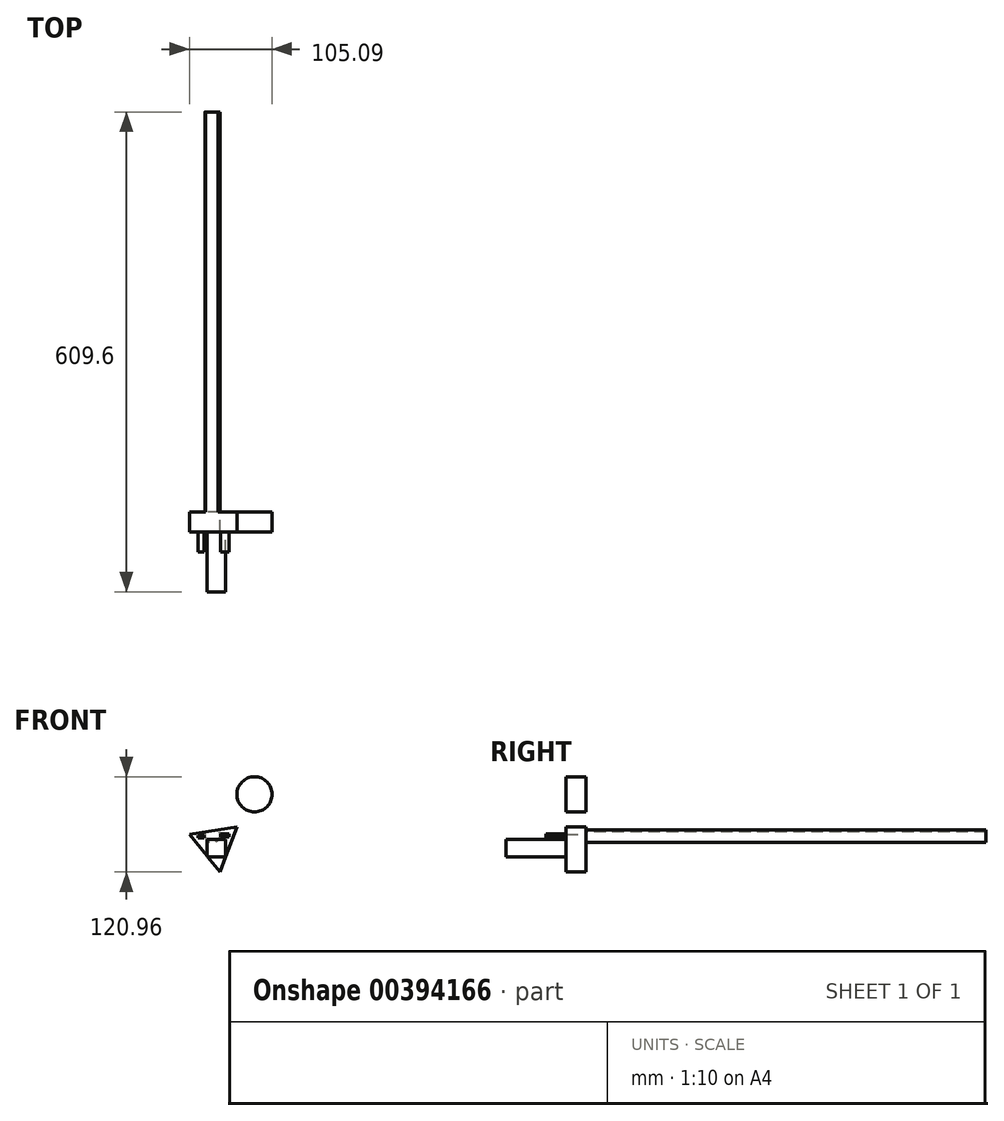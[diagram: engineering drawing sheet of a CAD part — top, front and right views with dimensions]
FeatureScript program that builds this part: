
annotation { "Feature Type Name" : "Feature", "Feature Type Description" : "" }
export const myFeature = defineFeature(function(context is Context, id is Id, definition is map)
    precondition{}
    {
        {
            var Q0;
            Q0=qCreatedBy(makeId("Front.planeOp"),FACE);
            var sketch = newSketch(context, id + "F0", { "sketchPlane" : qUnion([Q0])});
            skCircle(sketch, "E0", {"center": v(-39.51, 36.75) * mm, "radius": 31.41 * mm});
            skCircle(sketch, "E1", {"center": v(24.34, 44.64) * mm, "radius": 22.32 * mm});
            skSolve(sketch);
        }
        {
            var Q0;
            Q0=qCreatedBy(makeId("Front.planeOp"),FACE);
            var sketch = newSketch(context, id + "F1", { "sketchPlane" : qUnion([Q0])});
            skCircle(sketch, "E2.cCircle", {"center": v(-25.32, -19.02) * mm, "radius": 17.71 * mm, "construction": true});
            skLineSegment(sketch, "E2.0", {"start": v(2.15, 3.35) * mm, "end": v(-19.7, -54) * mm});
            skLineSegment(sketch, "E2.1", {"start": v(-19.7, -54) * mm, "end": v(-58.43, -6.4) * mm});
            skLineSegment(sketch, "E2.2", {"start": v(-58.43, -6.4) * mm, "end": v(2.15, 3.35) * mm});
            skPoint(sketch, "E2.0.midPoint", {"position": v(-8.77, -25.32) * mm});
            skCircle(sketch, "E3.cCircle", {"center": v(-112.43, 22.17) * mm, "radius": 6.09 * mm, "construction": true});
            skLineSegment(sketch, "E3.0", {"start": v(-124.6, 22.37) * mm, "end": v(-106.17, 32.61) * mm});
            skLineSegment(sketch, "E3.1", {"start": v(-106.17, 32.61) * mm, "end": v(-106.52, 11.53) * mm});
            skLineSegment(sketch, "E3.2", {"start": v(-106.52, 11.53) * mm, "end": v(-124.6, 22.37) * mm});
            skPoint(sketch, "E3.0.midPoint", {"position": v(-115.38, 27.5) * mm});
            skSolve(sketch);
        }
        {
            var Q0;
            Q0=makeQuery(id+"F0.imprint","IMPRINT",FACE,{"disambiguationData":[TD([[makeQuery(id+"F0.imprint","IMPRINT",EDGE,{"derivedFrom":sQuery(id+"F0.wireOp",EDGE,"E1")}),1.0]])]});
            var Q1;
            Q1=makeQuery(id+"F1.imprint","IMPRINT",FACE,{"disambiguationData":[TD([[makeQuery(id+"F1.imprint","IMPRINT",EDGE,{"derivedFrom":sQuery(id+"F1.wireOp",EDGE,"E2.0")}),-1.0]])]});
            extrude(context, id + "F2", {"entities" : qUnion([Q0, Q1]), "depth" : 25.4 * mm, "offsetDistance" : 25.4 * mm});
        }
        {
            var Q0;
            Q0=makeQuery(id+"F2.opExtrude","CAP_FACE",FACE,{"disambiguationData":[OSD([sQuery(id+"F1.wireOp",EDGE,"E2.0"),sQuery(id+"F1.wireOp",EDGE,"E2.1"),sQuery(id+"F1.wireOp",EDGE,"E2.2")])],"isStart":true});
            var sketch = newSketch(context, id + "F3", { "sketchPlane" : qUnion([Q0])});
            skCircle(sketch, "E4", {"center": v(28.98, -7.02) * mm, "radius": 9.53 * mm});
            skSolve(sketch);
        }
        {
            var Q0;
            {var subQ0=sQuery(id+"F3.wireOp",EDGE,"E4");var subQ1=makeQuery(id+"F2.opExtrude","CAP_EDGE",EDGE,{"disambiguationData":[OSD([sQuery(id+"F1.wireOp",EDGE,"E2.2")])],"isStart":true});var subQ2=makeQuery(id+"F3.imprint","INTERSECT",VERTEX,{"disambiguationData":[OD(0.0)],"derivedFrom":[subQ1,subQ0]});Q0=makeQuery(id+"F3.imprint","IMPRINT",FACE,{"disambiguationData":[TD([[makeQuery(id+"F3.imprint","IMPRINT",EDGE,{"disambiguationData":[TD([[subQ2,-1.0]])],"derivedFrom":subQ0}),1.0]])]});}
            extrude(context, id + "F4", {"entities" : qUnion([Q0]), "operationType" : NewBodyOperationType.ADD, "depth" : 508 * mm, "offsetDistance" : 25.4 * mm});
        }
        {
            var Q0;
            Q0=makeQuery(id+"F2.opExtrude","CAP_FACE",FACE,{"disambiguationData":[OSD([sQuery(id+"F1.wireOp",EDGE,"E2.0"),sQuery(id+"F1.wireOp",EDGE,"E2.1"),sQuery(id+"F1.wireOp",EDGE,"E2.2")])],"isStart":false});
            var sketch = newSketch(context, id + "F5", { "sketchPlane" : qUnion([Q0])});
            skLineSegment(sketch, "E5.bottom", {"start": v(-36.23, -12.63) * mm, "end": v(-12.5, -12.63) * mm});
            skLineSegment(sketch, "E5.top", {"start": v(-36.23, -35.1) * mm, "end": v(-12.5, -35.1) * mm});
            skLineSegment(sketch, "E5.left", {"start": v(-36.23, -12.63) * mm, "end": v(-36.23, -35.1) * mm});
            skLineSegment(sketch, "E5.right", {"start": v(-12.5, -12.63) * mm, "end": v(-12.5, -35.1) * mm});
            skSolve(sketch);
        }
        {
            var Q0;
            {var subQ1=sQuery(id+"F5.wireOp",EDGE,"E5.bottom");Q0=makeQuery(id+"F5.imprint","IMPRINT",FACE,{"disambiguationData":[TD([[makeQuery(id+"F5.imprint","IMPRINT",EDGE,{"derivedFrom":subQ1}),-1.0]])]});}
            extrude(context, id + "F6", {"entities" : qUnion([Q0]), "operationType" : NewBodyOperationType.ADD, "depth" : 76.2 * mm, "offsetDistance" : 25.4 * mm});
        }
        {
            var Q0;
            {var subQ0=sQuery(id+"F1.wireOp",EDGE,"E2.2");var subQ1=sQuery(id+"F1.wireOp",EDGE,"E2.1");var subQ2=sQuery(id+"F1.wireOp",EDGE,"E2.0");var subQ3=makeQuery(id+"F2.opExtrude","CAP_FACE",FACE,{"disambiguationData":[OSD([subQ2,subQ1,subQ0])],"isStart":false});Q0=makeQuery(id+"F6.boolean.opBoolean","SPLIT",FACE,{"disambiguationData":[TD([makeQuery(id+"F2.opExtrude","SWEPT_FACE",FACE,{"disambiguationData":[OSD([subQ2])]}),subQ3,makeQuery(id+"F2.opExtrude","SWEPT_FACE",FACE,{"disambiguationData":[OSD([subQ1])]}),makeQuery(id+"F2.opExtrude","SWEPT_FACE",FACE,{"disambiguationData":[OSD([subQ0])]}),makeQuery(id+"F4.opExtrude","SWEPT_FACE",FACE,{"disambiguationData":[OSD([subQ0])]}),makeQuery(id+"F6.opExtrude","SWEPT_FACE",FACE,{"disambiguationData":[OSD([sQuery(id+"F5.wireOp",EDGE,"E5.bottom")])]}),makeQuery(id+"F6.opExtrude","SWEPT_FACE",FACE,{"disambiguationData":[OSD([sQuery(id+"F5.wireOp",EDGE,"E5.top")])]}),makeQuery(id+"F6.opExtrude","SWEPT_FACE",FACE,{"disambiguationData":[OSD([sQuery(id+"F5.wireOp",EDGE,"E5.left")])]}),makeQuery(id+"F6.opExtrude","SWEPT_FACE",FACE,{"disambiguationData":[OSD([sQuery(id+"F5.wireOp",EDGE,"E5.right")])]}),makeQuery(id+"F6.opExtrude","SWEPT_FACE",FACE,{"disambiguationData":[OSD([subQ1])]})])],"derivedFrom":subQ3});}
            var sketch = newSketch(context, id + "F7", { "sketchPlane" : qUnion([Q0])});
            skLineSegment(sketch, "E6.bottom", {"start": v(-47.47, -7.47) * mm, "end": v(-39.91, -7.47) * mm});
            skLineSegment(sketch, "E6.top", {"start": v(-47.47, -10.42) * mm, "end": v(-39.91, -10.42) * mm});
            skLineSegment(sketch, "E6.left", {"start": v(-47.47, -7.47) * mm, "end": v(-47.47, -10.42) * mm});
            skLineSegment(sketch, "E6.right", {"start": v(-39.91, -7.47) * mm, "end": v(-39.91, -10.42) * mm});
            skLineSegment(sketch, "E7.bottom", {"start": v(-14.29, -4.89) * mm, "end": v(-6.73, -4.89) * mm});
            skLineSegment(sketch, "E7.top", {"start": v(-14.29, -7.47) * mm, "end": v(-6.73, -7.47) * mm});
            skLineSegment(sketch, "E7.left", {"start": v(-14.29, -4.89) * mm, "end": v(-14.29, -7.47) * mm});
            skLineSegment(sketch, "E7.right", {"start": v(-6.73, -4.89) * mm, "end": v(-6.73, -7.47) * mm});
            skSolve(sketch);
        }
        {
            var Q0;
            Q0=makeQuery(id+"F7.imprint","IMPRINT",FACE,{"disambiguationData":[TD([[makeQuery(id+"F7.imprint","IMPRINT",EDGE,{"derivedFrom":sQuery(id+"F7.wireOp",EDGE,"E6.bottom")}),-1.0]])]});
            extrude(context, id + "F8", {"entities" : qUnion([Q0]), "operationType" : NewBodyOperationType.ADD, "depth" : 25.4 * mm, "offsetDistance" : 25.4 * mm});
        }
        {
            var Q0;
            {var subQ0=sQuery(id+"F1.wireOp",EDGE,"E2.2");var subQ1=sQuery(id+"F1.wireOp",EDGE,"E2.1");var subQ2=sQuery(id+"F1.wireOp",EDGE,"E2.0");var subQ3=makeQuery(id+"F2.opExtrude","CAP_FACE",FACE,{"disambiguationData":[OSD([subQ2,subQ1,subQ0])],"isStart":false});Q0=makeQuery(id+"F6.boolean.opBoolean","SPLIT",FACE,{"disambiguationData":[TD([makeQuery(id+"F2.opExtrude","SWEPT_FACE",FACE,{"disambiguationData":[OSD([subQ2])]}),subQ3,makeQuery(id+"F2.opExtrude","SWEPT_FACE",FACE,{"disambiguationData":[OSD([subQ1])]}),makeQuery(id+"F2.opExtrude","SWEPT_FACE",FACE,{"disambiguationData":[OSD([subQ0])]}),makeQuery(id+"F4.opExtrude","SWEPT_FACE",FACE,{"disambiguationData":[OSD([subQ0])]}),makeQuery(id+"F6.opExtrude","SWEPT_FACE",FACE,{"disambiguationData":[OSD([sQuery(id+"F5.wireOp",EDGE,"E5.bottom")])]}),makeQuery(id+"F6.opExtrude","SWEPT_FACE",FACE,{"disambiguationData":[OSD([sQuery(id+"F5.wireOp",EDGE,"E5.top")])]}),makeQuery(id+"F6.opExtrude","SWEPT_FACE",FACE,{"disambiguationData":[OSD([sQuery(id+"F5.wireOp",EDGE,"E5.left")])]}),makeQuery(id+"F6.opExtrude","SWEPT_FACE",FACE,{"disambiguationData":[OSD([sQuery(id+"F5.wireOp",EDGE,"E5.right")])]}),makeQuery(id+"F6.opExtrude","SWEPT_FACE",FACE,{"disambiguationData":[OSD([subQ1])]})])],"derivedFrom":subQ3});}
            var sketch = newSketch(context, id + "F9", { "sketchPlane" : qUnion([Q0])});
            skLineSegment(sketch, "E8.bottom", {"start": v(-19.04, -5.78) * mm, "end": v(-8.02, -5.78) * mm});
            skLineSegment(sketch, "E8.top", {"start": v(-19.04, -9.12) * mm, "end": v(-8.02, -9.12) * mm});
            skLineSegment(sketch, "E8.left", {"start": v(-19.04, -5.78) * mm, "end": v(-19.04, -9.12) * mm});
            skLineSegment(sketch, "E8.right", {"start": v(-8.02, -5.78) * mm, "end": v(-8.02, -9.12) * mm});
            skSolve(sketch);
        }
        {
            var Q0;
            Q0=makeQuery(id+"F9.imprint","IMPRINT",FACE,{"disambiguationData":[TD([[makeQuery(id+"F9.imprint","IMPRINT",EDGE,{"derivedFrom":sQuery(id+"F9.wireOp",EDGE,"E8.bottom")}),-1.0]])]});
            extrude(context, id + "F10", {"entities" : qUnion([Q0]), "operationType" : NewBodyOperationType.ADD, "depth" : 25.4 * mm, "offsetDistance" : 25.4 * mm});
        }
    });
